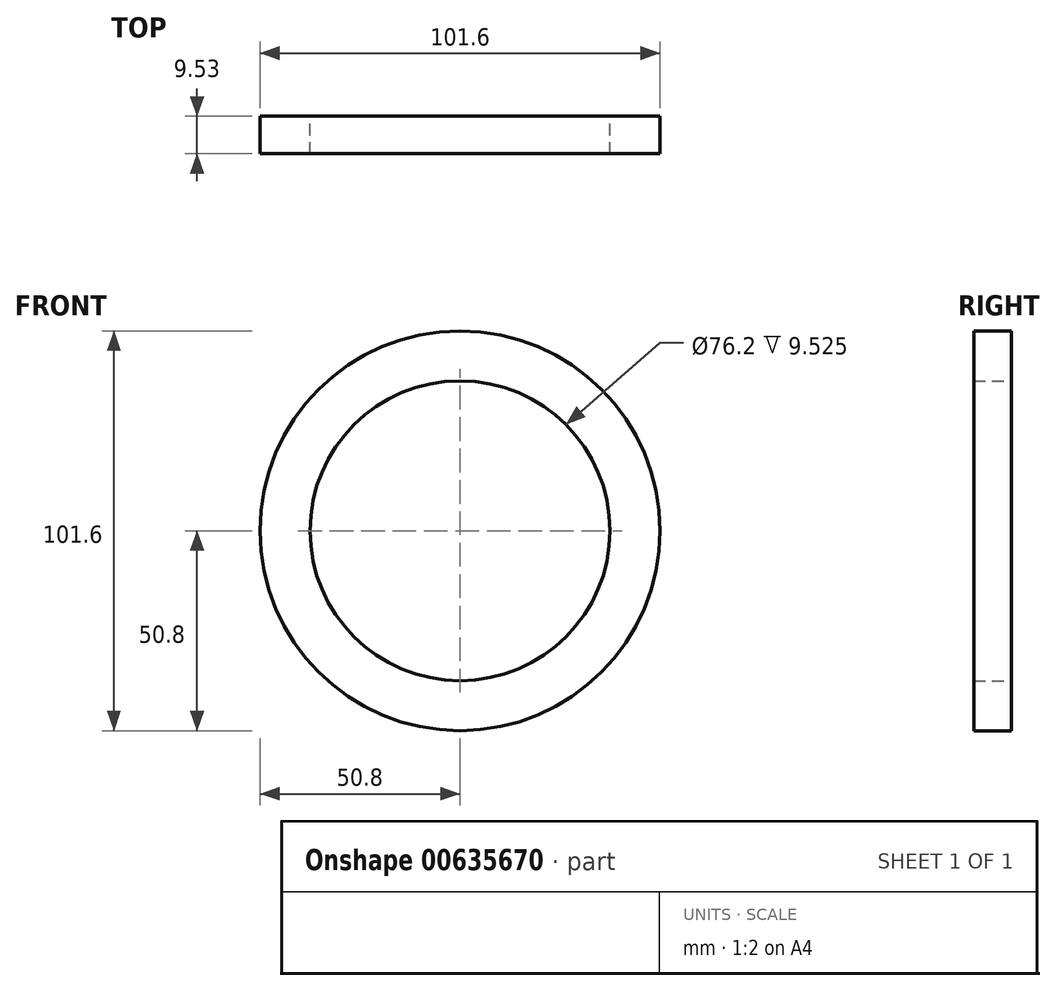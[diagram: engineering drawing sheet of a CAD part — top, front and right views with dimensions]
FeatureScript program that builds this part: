
annotation { "Feature Type Name" : "Feature", "Feature Type Description" : "" }
export const myFeature = defineFeature(function(context is Context, id is Id, definition is map)
    precondition{}
    {
        {
            var Q0;
            Q0=qCreatedBy(makeId("Front.planeOp"),FACE);
            var sketch = newSketch(context, id + "F0", { "sketchPlane" : qUnion([Q0])});
            skCircle(sketch, "E0", {"center": v(0, 0) * mm, "radius": 38.1 * mm});
            skCircle(sketch, "E1", {"center": v(0, 0) * mm, "radius": 50.8 * mm});
            skSolve(sketch);
        }
        {
            var Q0;
            Q0 = qSketchRegion(id + "F0", true);
            extrude(context, id + "F1", {"entities" : qUnion([Q0]), "depth" : 9.52 * mm, "offsetDistance" : 25.4 * mm});
        }
    });
